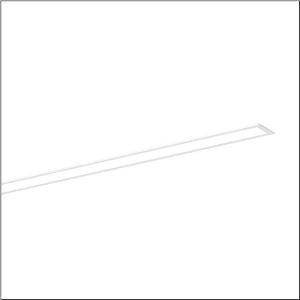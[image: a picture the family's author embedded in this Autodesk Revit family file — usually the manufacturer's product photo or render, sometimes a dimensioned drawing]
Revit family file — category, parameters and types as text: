
# Revit family: silica_r__21_51mx10dc35wb_43eb
name_source: partatom
category: Lighting Fixtures
units: mm (PartAtom-declared; Revit-internal decimal feet)

## family parameters
Cut with Voids When Loaded = No
Host = Face
Light Source = No
Part Type = Normal
Room Calculation Point = No
Round Connector Dimension = Use Diameter
Shared = No

## types (1)
- --- (1 x LED, 6000 lm, 42.6 W, 3000K)
    Apparent Load = 43 VA
    CIE Flux Codes = 48 79 96 100 100
    Color Rendering = 80
    Color Temperature = 3000K
    Default Elevation = 1800 mm
    Description = Silica® 21, office luminaire, primary optical cover: cover, of PMMA, opal, light emission: direct distribution, primary light characteristic: symmetric, installation type: recessed, LED, rated luminous flux: 6.000lm, luminous efficacy: 141lm/W, light colour: 830, colour temperature: 3000K, with terminal, 3+2-pole, max. 2.5mm², mains connection: 220..240V, AC, 50/60Hz, rated input power: 42.6W, luminaire housing, of aluminium, traffic white (RAL 9016), length: 3.028mm, width: 79mm, height: 53mm, protection rating (complete): IP20, insulation class (complete): insulation class I (protective earthing), certification: CE, permissible operating ambient temperature: 0..+35°C, standard: EN 50419, packaging unit: 1 piece
    Height = 0 mm  [stored 0 ft]
    Lamp = 1 x LED
    Lamp Light Flux = 6000 lm
    Lamp Power = 42.6 W
    Lamp count = 1
    Length = 3027 mm
    Luminous efficacy = 141 lm/W
    Manufacturer = Siteco
    ModVariant = No
    Model = 51MX10DC35WB
    Mounting Place = Ceiling
    Mounting Type = Recessed
    Number of Poles = 1
    OnlyDefault = Yes
    Power Factor = 1
    Product Name = Silica® 21
    Product group = office luminaire | ceiling recessed
    ProductGroupID = 401
    Protection Class = Protection class I
    Protection Degree = IP 20
    RLX_Detail_Level = 1
    RLX_Emergency_Light_Flux = 0 lm
    RLX_Emergency_Type = 0
    RLX_Emergency_Type_DB = No
    RlxData = <blob elided: 21217 chars, md5=9efa3be3>
    Socket = socket
    Standby Power = 0 W
    System Light Flux = 6000 lm
    System Power = 43 W
    Type Comments = factory setting: luminous flux: 100 % | dim-lin: 254 | 233 mA
    Type Image = l_1313615.jpg
    URL = http://relux.com
    VarID = @adj_065793
    Voltage = 0 V
    Weight = 0.00 kg
    Width = 79 mm

note: [stored X ft] marks values corroborated as IEEE doubles in the binary element streams (Revit-internal decimal feet)

## geometry (parser evidence)
native form markers: Blend x4, Sweep x12
no freeform markers — native parametric forms only
